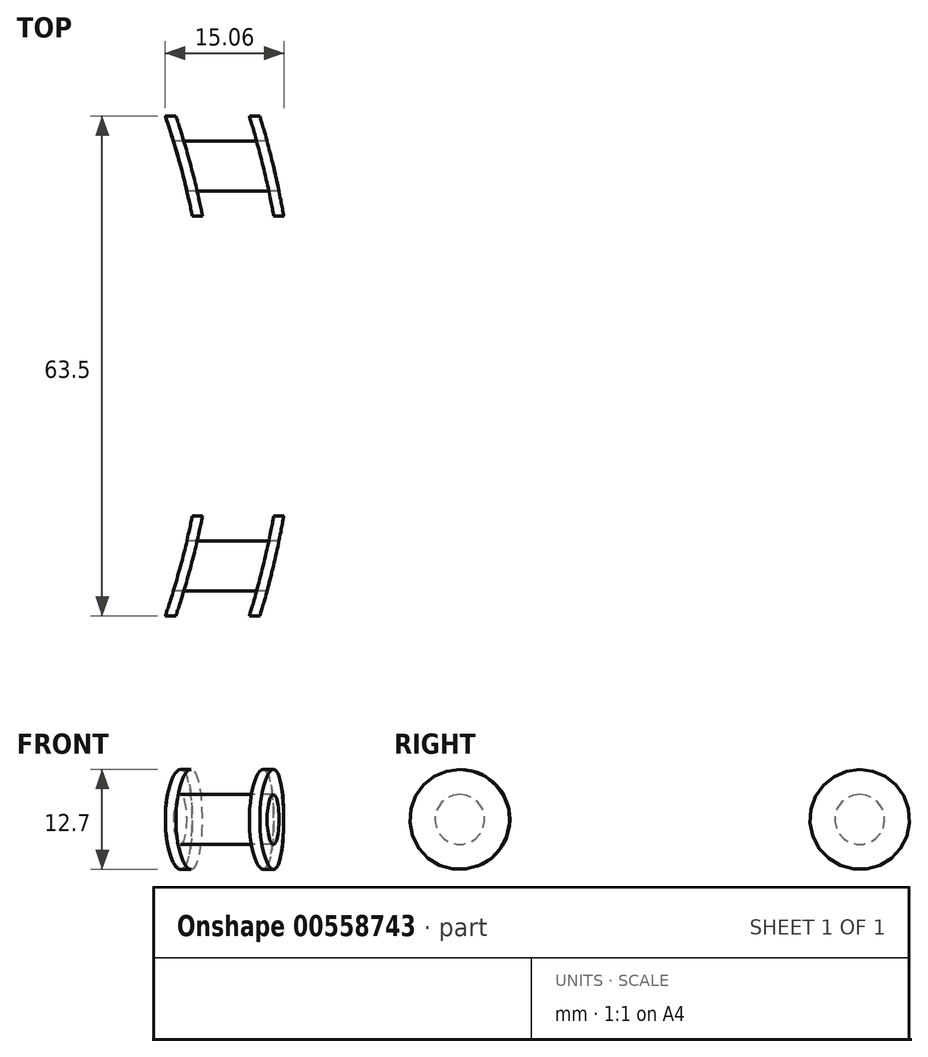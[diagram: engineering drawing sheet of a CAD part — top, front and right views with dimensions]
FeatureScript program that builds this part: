
annotation { "Feature Type Name" : "Feature", "Feature Type Description" : "" }
export const myFeature = defineFeature(function(context is Context, id is Id, definition is map)
    precondition{}
    {
        {
            var Q0;
            Q0=qCreatedBy(makeId("Right.planeOp"),FACE);
            var sketch = newSketch(context, id + "F0", { "sketchPlane" : qUnion([Q0])});
            skLineSegment(sketch, "E0", {"start": v(0, 0) * mm, "end": v(-25.4, 0) * mm});
            skLineSegment(sketch, "E1", {"start": v(-25.4, 0) * mm, "end": v(0, 0) * mm});
            skLineSegment(sketch, "E2", {"start": v(0, 0) * mm, "end": v(25.4, 0) * mm});
            skCircle(sketch, "E3", {"center": v(-25.4, 0) * mm, "radius": 3.18 * mm});
            skCircle(sketch, "E4", {"center": v(-25.4, 0) * mm, "radius": 6.35 * mm});
            skCircle(sketch, "E5", {"center": v(25.4, 0) * mm, "radius": 3.18 * mm});
            skCircle(sketch, "E6", {"center": v(25.4, 0) * mm, "radius": 6.35 * mm});
            skSolve(sketch);
        }
        {
            var Q0;
            Q0=qCreatedBy(makeId("Top.planeOp"),FACE);
            var sketch = newSketch(context, id + "F1", { "sketchPlane" : qUnion([Q0])});
            skCircle(sketch, "E7", {"center": v(0, 0) * mm, "radius": 107.95 * mm});
            skCircle(sketch, "E8", {"center": v(0, 0) * mm, "radius": 109.22 * mm});
            skCircle(sketch, "E9", {"center": v(0, 0) * mm, "radius": 99.06 * mm});
            skCircle(sketch, "E10", {"center": v(0, 0) * mm, "radius": 97.8 * mm});
            skCircle(sketch, "E11", {"center": v(0, 0) * mm, "radius": 152.4 * mm});
            skSolve(sketch);
        }
        {
            var Q0;
            Q0=makeQuery(id+"F1.imprint","IMPRINT",FACE,{"disambiguationData":[TD([[makeQuery(id+"F1.imprint","IMPRINT",EDGE,{"derivedFrom":sQuery(id+"F1.wireOp",EDGE,"E9")}),1.0]])]});
            var Q1;
            Q1=makeQuery(id+"F1.imprint","IMPRINT",FACE,{"disambiguationData":[TD([[makeQuery(id+"F1.imprint","IMPRINT",EDGE,{"derivedFrom":sQuery(id+"F1.wireOp",EDGE,"E7")}),-1.0]])]});
            extrude(context, id + "F2", {"entities" : qUnion([Q0, Q1]), "endBound" : BoundingType.SYMMETRIC, "depth" : 25.4 * mm, "offsetDistance" : 25.4 * mm});
        }
        {
            var Q0;
            Q0=makeQuery(id+"F0.imprint","IMPRINT",FACE,{"disambiguationData":[TD([[makeQuery(id+"F0.imprint","IMPRINT",EDGE,{"derivedFrom":sQuery(id+"F0.wireOp",EDGE,"E3")}),1.0]])]});
            var Q1;
            Q1=makeQuery(id+"F0.imprint","IMPRINT",FACE,{"disambiguationData":[TD([[makeQuery(id+"F0.imprint","IMPRINT",EDGE,{"derivedFrom":sQuery(id+"F0.wireOp",EDGE,"E3")}),-1.0]])]});
            var Q2;
            Q2=makeQuery(id+"F0.imprint","IMPRINT",FACE,{"disambiguationData":[TD([[makeQuery(id+"F0.imprint","IMPRINT",EDGE,{"derivedFrom":sQuery(id+"F0.wireOp",EDGE,"E5")}),1.0]])]});
            var Q3;
            Q3=makeQuery(id+"F0.imprint","IMPRINT",FACE,{"disambiguationData":[TD([[makeQuery(id+"F0.imprint","IMPRINT",EDGE,{"derivedFrom":sQuery(id+"F0.wireOp",EDGE,"E5")}),-1.0]])]});
            extrude(context, id + "F3", {"entities" : qUnion([Q0, Q1, Q2, Q3]), "operationType" : NewBodyOperationType.INTERSECT, "depth" : 208.28 * mm, "offsetDistance" : 25.4 * mm});
        }
        {
            var Q0;
            Q0=makeQuery(id+"F0.imprint","IMPRINT",FACE,{"disambiguationData":[TD([[makeQuery(id+"F0.imprint","IMPRINT",EDGE,{"derivedFrom":sQuery(id+"F0.wireOp",EDGE,"E3")}),1.0]])]});
            var Q1;
            Q1=makeQuery(id+"F0.imprint","IMPRINT",FACE,{"disambiguationData":[TD([[makeQuery(id+"F0.imprint","IMPRINT",EDGE,{"derivedFrom":sQuery(id+"F0.wireOp",EDGE,"E5")}),1.0]])]});
            extrude(context, id + "F4", {"entities" : qUnion([Q0, Q1]), "depth" : 113.03 * mm, "offsetDistance" : 25.4 * mm});
        }
        {
            var Q0;
            Q0=makeQuery(id+"F1.imprint","IMPRINT",FACE,{"disambiguationData":[TD([[makeQuery(id+"F1.imprint","IMPRINT",EDGE,{"derivedFrom":sQuery(id+"F1.wireOp",EDGE,"E10")}),1.0]])]});
            var Q1;
            Q1=makeQuery(id+"F1.imprint","IMPRINT",FACE,{"disambiguationData":[TD([[makeQuery(id+"F1.imprint","IMPRINT",EDGE,{"derivedFrom":sQuery(id+"F1.wireOp",EDGE,"E8")}),-1.0]])]});
            extrude(context, id + "F5", {"entities" : qUnion([Q0, Q1]), "operationType" : NewBodyOperationType.REMOVE, "endBound" : BoundingType.SYMMETRIC, "oppositeDirection" : true, "depth" : 25.4 * mm, "offsetDistance" : 25.4 * mm});
        }
    });
